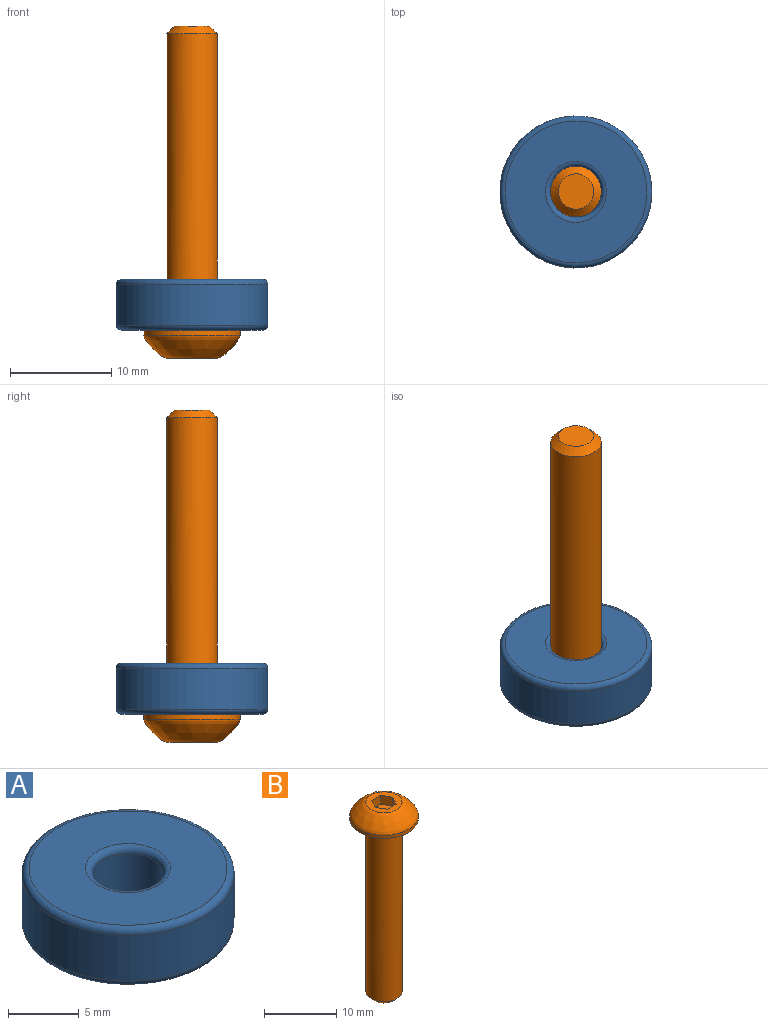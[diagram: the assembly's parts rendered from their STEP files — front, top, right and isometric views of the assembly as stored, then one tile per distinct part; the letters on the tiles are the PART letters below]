
ASSEMBLY  parts=2 mates=1
PART A: 8 faces, bbox 16.2x16.2x5 mm
  f0: cylinder r=2.5mm len=5mm, axis (0,0,-1), area 62.8mm2, adj f4,f6
  f1: cylinder r=7.5mm len=15mm, axis (0,0,-1), area 188.5mm2, adj f5,f7
  f2: plane 14x14mm, normal (0,0,1), area 125.7mm2, adj f6,f7
  f3: plane 14x14mm, normal (0,0,-1), area 125.7mm2, adj f4,f5
  f4: torus R=3mm, axis (0,0,1), area 13.2mm2, adj f0,f3
  f5: torus R=7mm, axis (0,0,1), area 36.1mm2, adj f1,f3
  f6: torus R=3mm, axis (0,0,1), area 13.2mm2, adj f0,f2
  f7: torus R=7mm, axis (0,0,1), area 36.1mm2, adj f1,f2
PART B: 14 faces, bbox 9.5x9.5x32.8 mm
  f0: plane 5.01x5.01mm, normal (0,0,1), area 11.8mm2, adj f3,f4,f5,f6,f7,f8,f10
  f1: cylinder r=4.75mm len=9.5mm, axis (0,0,-1), area 14.9mm2, adj f2,f10
  f2: plane 9.5x9.5mm, normal (0,0,-1), area 51.2mm2, adj f1,f11
  f3: plane 1.5x1.5mm, normal (-0.87,-0.5,0), area 2.6mm2, adj f0,f4,f8,f9
  f4: plane 1.73x1.5mm, normal (0,-1,0), area 2.6mm2, adj f0,f3,f5,f9
  f5: plane 1.5x1.5mm, normal (0.87,-0.5,0), area 2.6mm2, adj f0,f4,f6,f9
  f6: plane 1.5x1.5mm, normal (0.87,0.5,0), area 2.6mm2, adj f0,f5,f7,f9
  f7: plane 1.73x1.5mm, normal (0,1,0), area 2.6mm2, adj f0,f6,f8,f9
  f8: plane 1.5x1.5mm, normal (-0.87,0.5,0), area 2.6mm2, adj f0,f3,f7,f9
  f9: plane 3.46x3mm, normal (0,0,1), area 7.8mm2, adj f3,f4,f5,f6,f7,f8
  f10: bspline ~9.5x9.5mm, area 78.3mm2, adj f0,f1
  f11: cylinder r=2.5mm len=29.25mm, axis (0,0,1), area 459.5mm2, adj f2,f13
  f12: plane 3.5x3.5mm, normal (0,0,-1), area 9.6mm2, adj f13
  f13: cone r=1.75mm half-angle=45deg, axis (0,0,1), area 14.2mm2, adj f11,f12
PLACE A rot(axis=(1,0,0),180deg) t=(-13.81,-6.82,-4.04)mm
PLACE B rot(axis=(1,0,0),180deg) t=(48.69,-6.82,-9.04)mm
MATE fastened B.f1 <-> A.f0  axis (0,0,1) through (-13.81,-6.82,-9.04)mm
